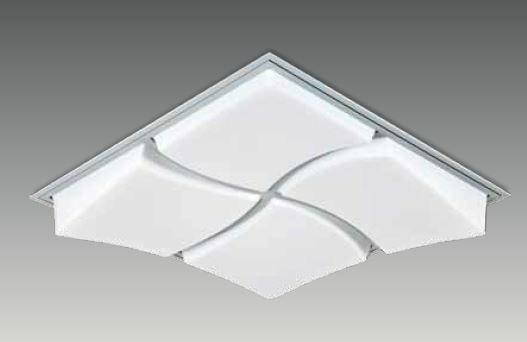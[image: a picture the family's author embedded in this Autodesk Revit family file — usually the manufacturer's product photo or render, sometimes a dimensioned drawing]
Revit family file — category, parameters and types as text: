
# Revit family: G 6060 LOP
name_source: partatom
category: Lighting Fixtures
revit_build: Autodesk Revit 2017 (Build: 20160225_1515(x64)
units: mm (PartAtom-declared; Revit-internal decimal feet)

## family parameters
Always vertical = Yes
Cut with Voids When Loaded = No
Host = Ceiling
Light Source = Yes
OmniClass Number = 23.80.70.11
OmniClass Title = Luminaries for Internal Lighting
Part Type = Normal
Room Calculation Point = No
Round Connector Dimension = Use Diameter
Shared = No

## types (4) — shared parameters
Color Filter = 16777215
Dimming Lamp Color Temperature Shift = <None>
Emit Shape Visible in Rendering = No
Emit from Rectangle Length = 540 mm  [stored 1.77165 ft]
Emit from Rectangle Width = 540 mm  [stored 1.77165 ft]
Light Source Symbol Size = 610 mm
Manufacturer = ARLIGHT
Type Image = G 6060 LOP.JPG

## per-type parameters (varying)
| type | Apparent Load | Wattage Comments |
| GLOP.6060.36.30 | 0 VA | 36 |
| GLOP.6060.36.40 | 0 VA | 36W |
| GLOP.6060.28.30 | 0 VA | 28 |
| GLOP.6060.28.40 | 28 VA | 28W |

note: [stored X ft] marks values corroborated as IEEE doubles in the binary element streams (Revit-internal decimal feet)

## geometry (parser evidence)
native form markers: Sweep x2
no freeform markers — native parametric forms only
